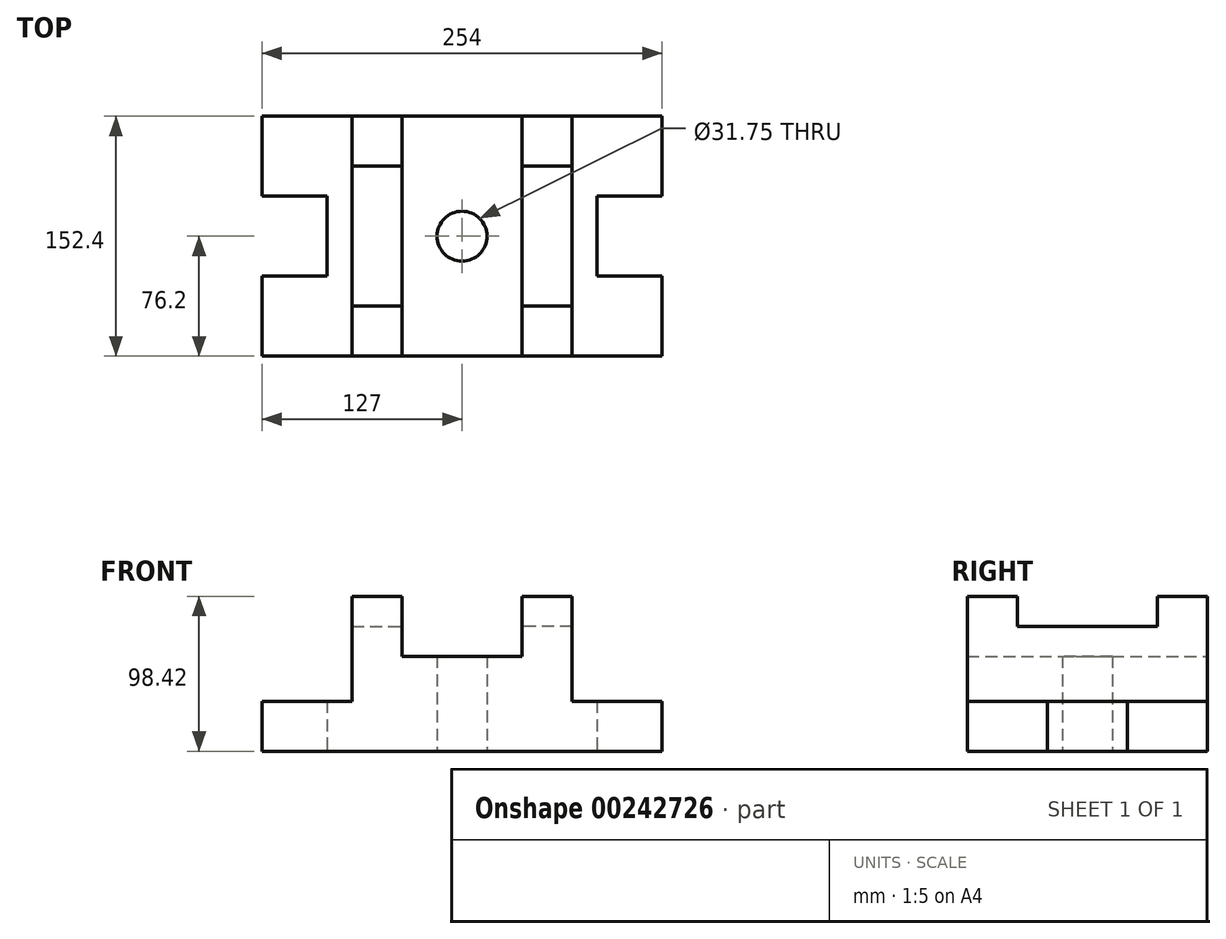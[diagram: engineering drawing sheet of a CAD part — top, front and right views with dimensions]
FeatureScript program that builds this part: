
annotation { "Feature Type Name" : "Feature", "Feature Type Description" : "" }
export const myFeature = defineFeature(function(context is Context, id is Id, definition is map)
    precondition{}
    {
        {
            var Q0;
            Q0=qCreatedBy(makeId("Top.planeOp"),FACE);
            var sketch = newSketch(context, id + "F0", { "sketchPlane" : qUnion([Q0])});
            skLineSegment(sketch, "E0.bottom", {"start": v(127, -76.2) * mm, "end": v(-127, -76.2) * mm});
            skLineSegment(sketch, "E0.top", {"start": v(127, 76.2) * mm, "end": v(-127, 76.2) * mm});
            skLineSegment(sketch, "E0.left", {"start": v(127, -76.2) * mm, "end": v(127, -25.4) * mm});
            skLineSegment(sketch, "E0.right", {"start": v(-127, -76.2) * mm, "end": v(-127, -25.4) * mm});
            skPoint(sketch, "E0.middle", {"position": v(0, 0) * mm});
            skLineSegment(sketch, "E1", {"start": v(85.72, -25.4) * mm, "end": v(127, -25.4) * mm});
            skLineSegment(sketch, "E2", {"start": v(85.72, 25.4) * mm, "end": v(127, 25.4) * mm});
            skLineSegment(sketch, "E3", {"start": v(85.72, 25.4) * mm, "end": v(85.72, -25.4) * mm});
            skLineSegment(sketch, "E4", {"start": v(69.85, 76.2) * mm, "end": v(69.85, -76.2) * mm});
            skLineSegment(sketch, "E5", {"start": v(38.1, 76.2) * mm, "end": v(38.1, -76.2) * mm});
            skLineSegment(sketch, "E6", {"start": v(-127, 25.4) * mm, "end": v(-85.72, 25.4) * mm});
            skLineSegment(sketch, "E7", {"start": v(-85.72, 25.4) * mm, "end": v(-85.72, -25.4) * mm});
            skLineSegment(sketch, "E8", {"start": v(-85.72, -25.4) * mm, "end": v(-127, -25.4) * mm});
            skLineSegment(sketch, "E9", {"start": v(-69.85, 76.2) * mm, "end": v(-69.85, -76.2) * mm});
            skLineSegment(sketch, "E10", {"start": v(-38.1, 76.2) * mm, "end": v(-38.1, -76.2) * mm});
            skCircle(sketch, "E11", {"center": v(0, 0) * mm, "radius": 15.88 * mm});
            skLineSegment(sketch, "E12", {"start": v(-69.85, -44.45) * mm, "end": v(-38.1, -44.45) * mm});
            skLineSegment(sketch, "E13", {"start": v(-69.85, 44.45) * mm, "end": v(-38.1, 44.45) * mm});
            skLineSegment(sketch, "E14", {"start": v(38.1, -44.45) * mm, "end": v(69.85, -44.45) * mm});
            skLineSegment(sketch, "E15", {"start": v(69.85, -44.45) * mm, "end": v(69.85, 44.45) * mm});
            skLineSegment(sketch, "E16", {"start": v(69.85, 44.45) * mm, "end": v(38.1, 44.45) * mm});
            skLineSegment(sketch, "E17.trimOffspring", {"start": v(127, 25.4) * mm, "end": v(127, 76.2) * mm});
            skLineSegment(sketch, "E18.trimOffspring", {"start": v(-127, 25.4) * mm, "end": v(-127, 76.2) * mm});
            skSolve(sketch);
        }
        {
            var Q0;
            {var subQ3=sQuery(id+"F0.wireOp",EDGE,"E6");Q0=makeQuery(id+"F0.imprint","IMPRINT",FACE,{"disambiguationData":[TD([[makeQuery(id+"F0.imprint","IMPRINT",EDGE,{"derivedFrom":subQ3}),1.0]])]});}
            var Q1;
            {var subQ0=sQuery(id+"F0.wireOp",EDGE,"E12");Q1=makeQuery(id+"F0.imprint","IMPRINT",FACE,{"disambiguationData":[TD([[makeQuery(id+"F0.imprint","IMPRINT",EDGE,{"derivedFrom":subQ0}),1.0]])]});}
            var Q2;
            {var subQ5=sQuery(id+"F0.wireOp",EDGE,"E13");Q2=makeQuery(id+"F0.imprint","IMPRINT",FACE,{"disambiguationData":[TD([[makeQuery(id+"F0.imprint","IMPRINT",EDGE,{"derivedFrom":subQ5}),1.0]])]});}
            var Q3;
            Q3=makeQuery(id+"F0.imprint","IMPRINT",FACE,{"disambiguationData":[TD([[makeQuery(id+"F0.imprint","IMPRINT",EDGE,{"derivedFrom":sQuery(id+"F0.wireOp",EDGE,"E11")}),-1.0]])]});
            var Q4;
            {var subQ0=sQuery(id+"F0.wireOp",EDGE,"E14");Q4=makeQuery(id+"F0.imprint","IMPRINT",FACE,{"disambiguationData":[TD([[makeQuery(id+"F0.imprint","IMPRINT",EDGE,{"derivedFrom":subQ0}),1.0]])]});}
            var Q5;
            {var subQ5=sQuery(id+"F0.wireOp",EDGE,"E14");Q5=makeQuery(id+"F0.imprint","IMPRINT",FACE,{"disambiguationData":[TD([[makeQuery(id+"F0.imprint","IMPRINT",EDGE,{"derivedFrom":subQ5}),-1.0]])]});}
            var Q6;
            {var subQ6=sQuery(id+"F0.wireOp",EDGE,"E1");Q6=makeQuery(id+"F0.imprint","IMPRINT",FACE,{"disambiguationData":[TD([[makeQuery(id+"F0.imprint","IMPRINT",EDGE,{"derivedFrom":subQ6}),-1.0]])]});}
            var Q7;
            {var subQ5=sQuery(id+"F0.wireOp",EDGE,"E16");Q7=makeQuery(id+"F0.imprint","IMPRINT",FACE,{"disambiguationData":[TD([[makeQuery(id+"F0.imprint","IMPRINT",EDGE,{"derivedFrom":subQ5}),-1.0]])]});}
            var Q8;
            {var subQ5=sQuery(id+"F0.wireOp",EDGE,"E12");Q8=makeQuery(id+"F0.imprint","IMPRINT",FACE,{"disambiguationData":[TD([[makeQuery(id+"F0.imprint","IMPRINT",EDGE,{"derivedFrom":subQ5}),-1.0]])]});}
            extrude(context, id + "F1", {"entities" : qUnion([Q0, Q1, Q2, Q3, Q4, Q5, Q6, Q7, Q8]), "depth" : 31.75 * mm});
        }
        {
            var Q0;
            {var subQ5=sQuery(id+"F0.wireOp",EDGE,"E12");Q0=makeQuery(id+"F0.imprint","IMPRINT",FACE,{"disambiguationData":[TD([[makeQuery(id+"F0.imprint","IMPRINT",EDGE,{"derivedFrom":subQ5}),-1.0]])]});}
            var Q1;
            {var subQ0=sQuery(id+"F0.wireOp",EDGE,"E12");Q1=makeQuery(id+"F0.imprint","IMPRINT",FACE,{"disambiguationData":[TD([[makeQuery(id+"F0.imprint","IMPRINT",EDGE,{"derivedFrom":subQ0}),1.0]])]});}
            var Q2;
            {var subQ5=sQuery(id+"F0.wireOp",EDGE,"E13");Q2=makeQuery(id+"F0.imprint","IMPRINT",FACE,{"disambiguationData":[TD([[makeQuery(id+"F0.imprint","IMPRINT",EDGE,{"derivedFrom":subQ5}),1.0]])]});}
            var Q3;
            Q3=makeQuery(id+"F0.imprint","IMPRINT",FACE,{"disambiguationData":[TD([[makeQuery(id+"F0.imprint","IMPRINT",EDGE,{"derivedFrom":sQuery(id+"F0.wireOp",EDGE,"E11")}),-1.0]])]});
            var Q4;
            {var subQ5=sQuery(id+"F0.wireOp",EDGE,"E16");Q4=makeQuery(id+"F0.imprint","IMPRINT",FACE,{"disambiguationData":[TD([[makeQuery(id+"F0.imprint","IMPRINT",EDGE,{"derivedFrom":subQ5}),-1.0]])]});}
            var Q5;
            {var subQ0=sQuery(id+"F0.wireOp",EDGE,"E14");Q5=makeQuery(id+"F0.imprint","IMPRINT",FACE,{"disambiguationData":[TD([[makeQuery(id+"F0.imprint","IMPRINT",EDGE,{"derivedFrom":subQ0}),1.0]])]});}
            var Q6;
            {var subQ5=sQuery(id+"F0.wireOp",EDGE,"E14");Q6=makeQuery(id+"F0.imprint","IMPRINT",FACE,{"disambiguationData":[TD([[makeQuery(id+"F0.imprint","IMPRINT",EDGE,{"derivedFrom":subQ5}),-1.0]])]});}
            extrude(context, id + "F2", {"entities" : qUnion([Q0, Q1, Q2, Q3, Q4, Q5, Q6]), "operationType" : NewBodyOperationType.ADD, "depth" : 60.32 * mm});
        }
        {
            var Q0;
            {var subQ0=sQuery(id+"F0.wireOp",EDGE,"E12");Q0=makeQuery(id+"F0.imprint","IMPRINT",FACE,{"disambiguationData":[TD([[makeQuery(id+"F0.imprint","IMPRINT",EDGE,{"derivedFrom":subQ0}),1.0]])]});}
            var Q1;
            {var subQ0=sQuery(id+"F0.wireOp",EDGE,"E14");Q1=makeQuery(id+"F0.imprint","IMPRINT",FACE,{"disambiguationData":[TD([[makeQuery(id+"F0.imprint","IMPRINT",EDGE,{"derivedFrom":subQ0}),1.0]])]});}
            extrude(context, id + "F3", {"entities" : qUnion([Q0, Q1]), "operationType" : NewBodyOperationType.ADD, "depth" : 79.38 * mm});
        }
        {
            var Q0;
            {var subQ5=sQuery(id+"F0.wireOp",EDGE,"E13");Q0=makeQuery(id+"F0.imprint","IMPRINT",FACE,{"disambiguationData":[TD([[makeQuery(id+"F0.imprint","IMPRINT",EDGE,{"derivedFrom":subQ5}),1.0]])]});}
            var Q1;
            {var subQ5=sQuery(id+"F0.wireOp",EDGE,"E12");Q1=makeQuery(id+"F0.imprint","IMPRINT",FACE,{"disambiguationData":[TD([[makeQuery(id+"F0.imprint","IMPRINT",EDGE,{"derivedFrom":subQ5}),-1.0]])]});}
            var Q2;
            {var subQ5=sQuery(id+"F0.wireOp",EDGE,"E14");Q2=makeQuery(id+"F0.imprint","IMPRINT",FACE,{"disambiguationData":[TD([[makeQuery(id+"F0.imprint","IMPRINT",EDGE,{"derivedFrom":subQ5}),-1.0]])]});}
            var Q3;
            {var subQ5=sQuery(id+"F0.wireOp",EDGE,"E16");Q3=makeQuery(id+"F0.imprint","IMPRINT",FACE,{"disambiguationData":[TD([[makeQuery(id+"F0.imprint","IMPRINT",EDGE,{"derivedFrom":subQ5}),-1.0]])]});}
            extrude(context, id + "F4", {"entities" : qUnion([Q0, Q1, Q2, Q3]), "operationType" : NewBodyOperationType.ADD, "depth" : 98.42 * mm});
        }
    });
